# Revit family: R37K
name_source: partatom
category: Pipe Accessories
units: mm (PartAtom-declared; Revit-internal decimal feet)

## family parameters
Always vertical = No
Cut with Voids When Loaded = No
Part Type = Normal
Round Connector Dimension = Use Diameter
Shared = Yes
Work Plane-Based = Yes

## types (2) — shared parameters
Default Elevation = 1219 mm
Manufacturer = Giacomini
Series = R37K

## per-type parameters (varying)
| type | Code | H1 | H2 | Height | Nut Dimension 1 | Nut dimension 2 | R1 |
| G 1-1/4”F x calotta G 2”F | R37KY006 | 16 mm | 6 mm  [stored 0.019685 ft] | 33 mm | 63 mm | 46 mm | 29 mm |
| G 1”F x calotta G 1-1/2”F | R37KY005 | 15 mm | 7 mm  [stored 0.0229659 ft] | 27 mm | 51 mm | 38 mm | 23 mm |

note: column(s) folded — value = type name in every type: Model

note: [stored X ft] marks values corroborated as IEEE doubles in the binary element streams (Revit-internal decimal feet)

## geometry (parser evidence)
native form markers: Sweep x3
no freeform markers — native parametric forms only
